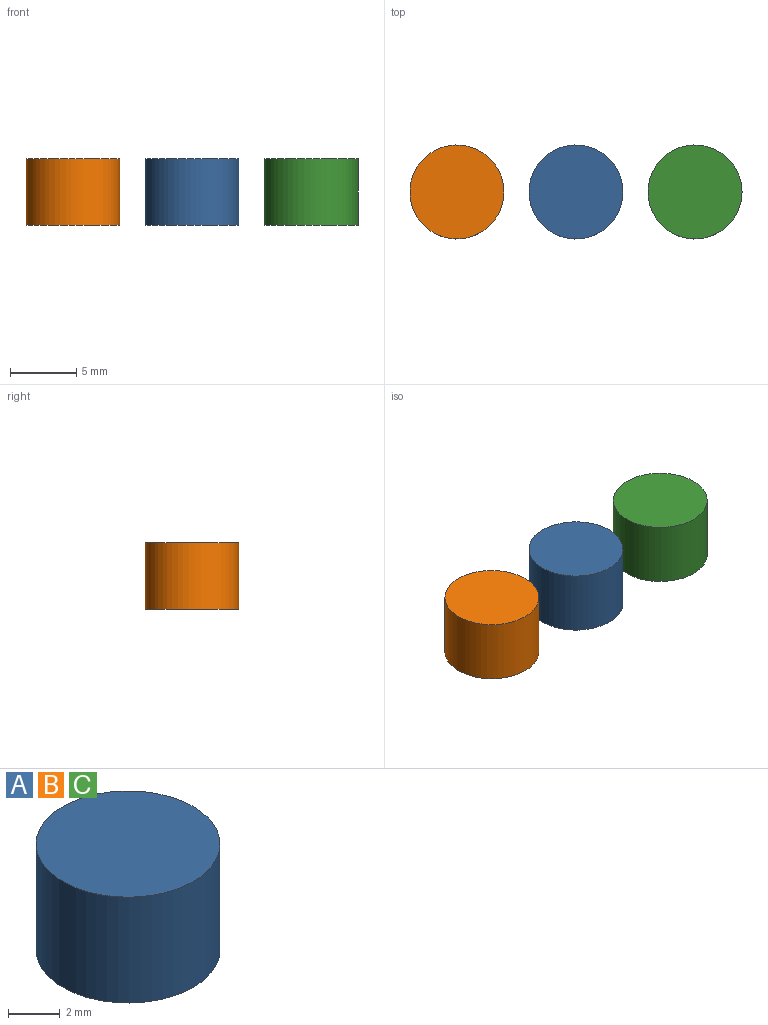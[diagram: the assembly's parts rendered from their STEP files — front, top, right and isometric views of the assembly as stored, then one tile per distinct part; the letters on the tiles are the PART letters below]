
ASSEMBLY  parts=3 mates=2
PART A: 3 faces, bbox 7.1x7.1x5 mm
  f0: cylinder r=3.55mm len=7.1mm, axis (0,0,-1), area 111.5mm2, adj f1,f2
  f1: plane 7.1x7.1mm, normal (0,0,1), area 39.6mm2, adj f0
  f2: plane 7.1x7.1mm, normal (0,0,-1), area 39.6mm2, adj f0
PART B: same geometry as A
PART C: same geometry as A
PLACE A t=(9,0,0)mm
PLACE B at identity
PLACE C t=(18,0,0)mm
MATE fastened C.f0 <-> A.f2  axis (0,0,-1) through (18,0,0)mm
MATE fastened A.f0 <-> B.f2  axis (0,0,-1) through (9,0,0)mm
